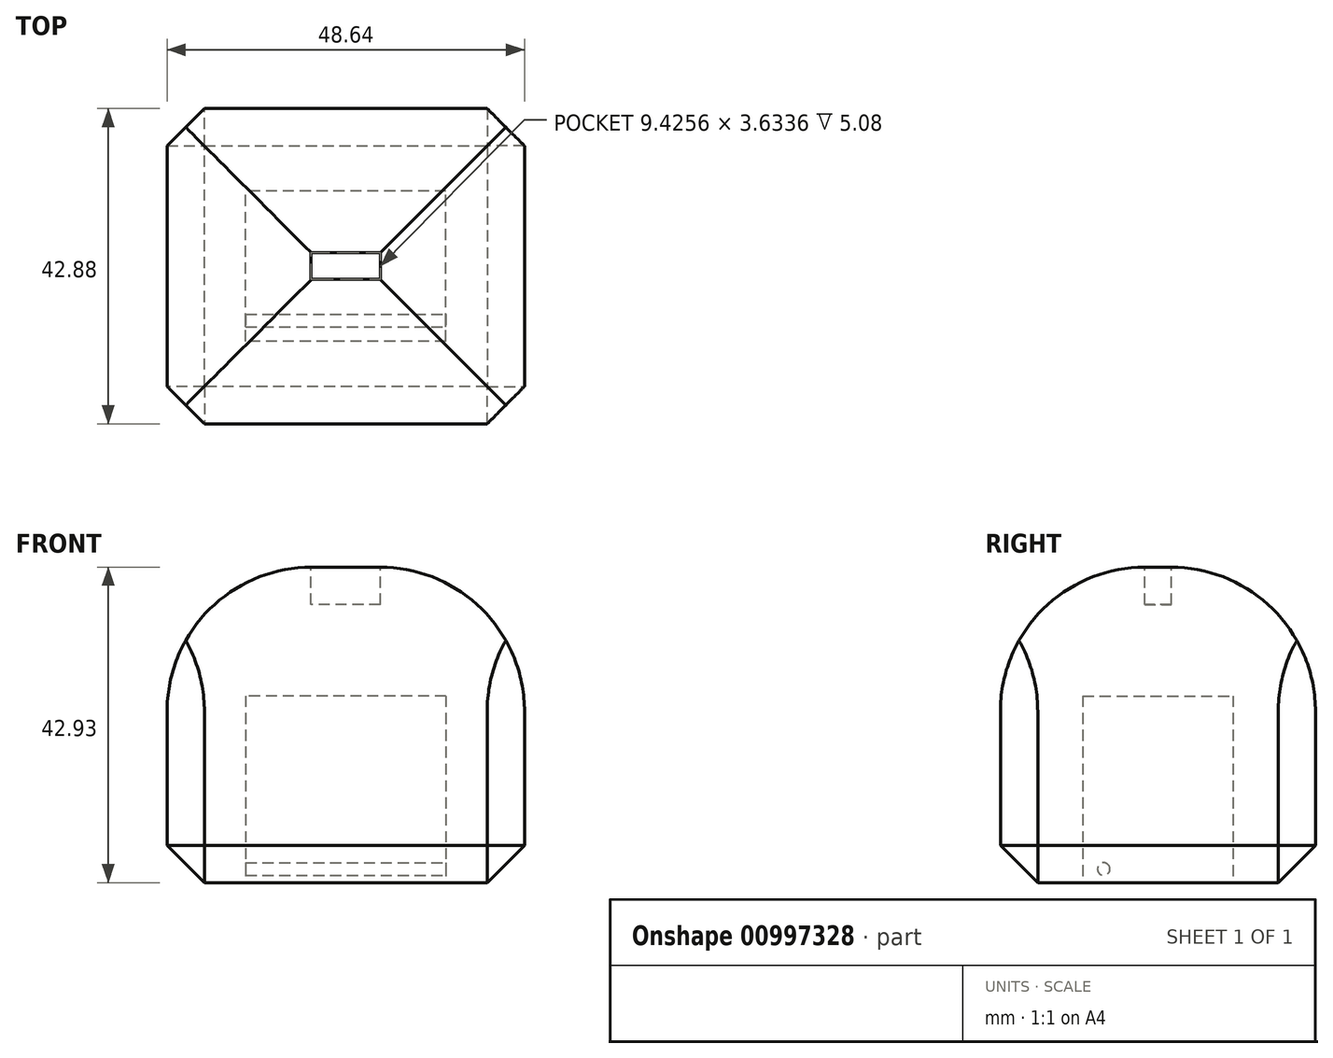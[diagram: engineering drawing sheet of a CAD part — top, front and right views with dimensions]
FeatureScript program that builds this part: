
annotation { "Feature Type Name" : "Feature", "Feature Type Description" : "" }
export const myFeature = defineFeature(function(context is Context, id is Id, definition is map)
    precondition{}
    {
        {
            var Q0;
            Q0=qCreatedBy(makeId("Top.planeOp"),FACE);
            var sketch = newSketch(context, id + "F0", { "sketchPlane" : qUnion([Q0])});
            skLineSegment(sketch, "E0.bottom", {"start": v(24.32, 21.44) * mm, "end": v(-24.32, 21.44) * mm});
            skLineSegment(sketch, "E0.top", {"start": v(24.32, -21.44) * mm, "end": v(-24.32, -21.44) * mm});
            skLineSegment(sketch, "E0.left", {"start": v(24.32, 21.44) * mm, "end": v(24.32, -21.44) * mm});
            skLineSegment(sketch, "E0.right", {"start": v(-24.32, 21.44) * mm, "end": v(-24.32, -21.44) * mm});
            skPoint(sketch, "E0.middle", {"position": v(0, 0) * mm});
            skSolve(sketch);
        }
        {
            var Q0;
            Q0 = qSketchRegion(id + "F0", true);
            extrude(context, id + "F1", {"entities" : qUnion([Q0]), "depth" : 42.93 * mm, "offsetDistance" : 25.4 * mm});
        }
        {
            var Q0;
            Q0=makeQuery(id+"F1.opExtrude","CAP_EDGE",EDGE,{"disambiguationData":[OSD([sQuery(id+"F0.wireOp",EDGE,"E0.left")])],"isStart":false});
            var Q1;
            Q1=makeQuery(id+"F1.opExtrude","CAP_EDGE",EDGE,{"disambiguationData":[OSD([sQuery(id+"F0.wireOp",EDGE,"E0.top")])],"isStart":false});
            var Q2;
            Q2=makeQuery(id+"F1.opExtrude","CAP_EDGE",EDGE,{"disambiguationData":[OSD([sQuery(id+"F0.wireOp",EDGE,"E0.bottom")])],"isStart":false});
            var Q3;
            Q3=makeQuery(id+"F1.opExtrude","CAP_EDGE",EDGE,{"disambiguationData":[OSD([sQuery(id+"F0.wireOp",EDGE,"E0.right")])],"isStart":false});
            fillet(context, id + "F2", {"entities" : qUnion([Q0, Q1, Q2, Q3]), "radius" : 19.62 * mm, "tangentPropagation" : true, "allowEdgeOverflow" : false});
        }
        {
            var Q0;
            Q0=makeQuery(id+"F1.opExtrude","CAP_FACE",FACE,{"disambiguationData":[OSD([sQuery(id+"F0.wireOp",EDGE,"E0.bottom"),sQuery(id+"F0.wireOp",EDGE,"E0.top"),sQuery(id+"F0.wireOp",EDGE,"E0.left"),sQuery(id+"F0.wireOp",EDGE,"E0.right")])],"isStart":false});
            cPlane(context, id + "F3", {"entities" : qUnion([Q0]), "cplaneType" : CPlaneType.OFFSET, "offset" : 0 * mm, "width" : 152.4 * mm, "height" : 152.4 * mm});
        }
        {
            var Q0;
            Q0=qCreatedBy(id+"F3.planeOp",FACE);
            var sketch = newSketch(context, id + "F4", { "sketchPlane" : qUnion([Q0])});
            skLineSegment(sketch, "E1", {"start": v(-4.71, 1.83) * mm, "end": v(-4.71, -1.8) * mm});
            skLineSegment(sketch, "E2", {"start": v(-4.71, -1.8) * mm, "end": v(4.71, -1.8) * mm});
            skLineSegment(sketch, "E3", {"start": v(4.71, -1.8) * mm, "end": v(4.71, 1.82) * mm});
            skLineSegment(sketch, "E4", {"start": v(4.71, 1.82) * mm, "end": v(-4.71, 1.83) * mm});
            skSolve(sketch);
        }
        {
            var Q0;
            Q0=makeQuery(id+"F4.imprint","IMPRINT",FACE,{"disambiguationData":[TD([[makeQuery(id+"F4.imprint","IMPRINT",EDGE,{"derivedFrom":sQuery(id+"F4.wireOp",EDGE,"E1")}),1.0]])]});
            extrude(context, id + "F5", {"entities" : qUnion([Q0]), "operationType" : NewBodyOperationType.REMOVE, "oppositeDirection" : true, "depth" : 5.08 * mm, "offsetDistance" : 25.4 * mm});
        }
        {
            var Q0;
            Q0=makeQuery(id+"F1.opExtrude","CAP_FACE",FACE,{"disambiguationData":[OSD([sQuery(id+"F0.wireOp",EDGE,"E0.bottom"),sQuery(id+"F0.wireOp",EDGE,"E0.top"),sQuery(id+"F0.wireOp",EDGE,"E0.left"),sQuery(id+"F0.wireOp",EDGE,"E0.right")])],"isStart":true});
            var Q1;
            Q1=makeQuery(id+"F1.opExtrude","SWEPT_FACE",FACE,{"disambiguationData":[OSD([sQuery(id+"F0.wireOp",EDGE,"E0.right")])]});
            var Q2;
            Q2=makeQuery(id+"F1.opExtrude","SWEPT_FACE",FACE,{"disambiguationData":[OSD([sQuery(id+"F0.wireOp",EDGE,"E0.top")])]});
            var Q3;
            Q3=makeQuery(id+"F1.opExtrude","SWEPT_FACE",FACE,{"disambiguationData":[OSD([sQuery(id+"F0.wireOp",EDGE,"E0.left")])]});
            var Q4;
            Q4=makeQuery(id+"F1.opExtrude","SWEPT_FACE",FACE,{"disambiguationData":[OSD([sQuery(id+"F0.wireOp",EDGE,"E0.bottom")])]});
            chamfer(context, id + "F6", {"entities" : qUnion([Q0, Q1, Q2, Q3, Q4]), "width" : 5.08 * mm, "tangentPropagation" : true});
        }
        {
            var Q0;
            Q0=makeQuery(id+"F1.opExtrude","CAP_FACE",FACE,{"disambiguationData":[OSD([sQuery(id+"F0.wireOp",EDGE,"E0.bottom"),sQuery(id+"F0.wireOp",EDGE,"E0.top"),sQuery(id+"F0.wireOp",EDGE,"E0.left"),sQuery(id+"F0.wireOp",EDGE,"E0.right")])],"isStart":true});
            var sketch = newSketch(context, id + "F7", { "sketchPlane" : qUnion([Q0])});
            skLineSegment(sketch, "E5.bottom", {"start": v(13.63, 10.22) * mm, "end": v(-13.63, 10.22) * mm});
            skLineSegment(sketch, "E5.top", {"start": v(13.63, -10.22) * mm, "end": v(-13.63, -10.22) * mm});
            skLineSegment(sketch, "E5.left", {"start": v(13.63, 10.22) * mm, "end": v(13.63, -10.22) * mm});
            skLineSegment(sketch, "E5.right", {"start": v(-13.63, 10.22) * mm, "end": v(-13.63, -10.22) * mm});
            skPoint(sketch, "E5.middle", {"position": v(0, 0) * mm});
            skSolve(sketch);
        }
        {
            var Q0;
            Q0=makeQuery(id+"F7.imprint","IMPRINT",FACE,{"disambiguationData":[TD([[makeQuery(id+"F7.imprint","IMPRINT",EDGE,{"derivedFrom":sQuery(id+"F7.wireOp",EDGE,"E5.bottom")}),1.0]])]});
            extrude(context, id + "F8", {"entities" : qUnion([Q0]), "operationType" : NewBodyOperationType.REMOVE, "oppositeDirection" : true, "depth" : 25.4 * mm, "offsetDistance" : 25.4 * mm});
        }
        {
            var Q0;
            Q0=makeQuery(id+"F8.boolean.opBoolean","COPY",FACE,{"derivedFrom":makeQuery(id+"F8.opExtrude","SWEPT_FACE",FACE,{"disambiguationData":[OSD([sQuery(id+"F7.wireOp",EDGE,"E5.left")])]})});
            var sketch = newSketch(context, id + "F9", { "sketchPlane" : qUnion([Q0])});
            skCircle(sketch, "E6", {"center": v(7.38, 1.85) * mm, "radius": 0.85 * mm});
            skSolve(sketch);
        }
        {
            var Q0;
            Q0 = qSketchRegion(id + "F9", true);
            extrude(context, id + "F10", {"entities" : qUnion([Q0]), "operationType" : NewBodyOperationType.ADD, "depth" : 27.48 * mm, "offsetDistance" : 25.4 * mm});
        }
    });
